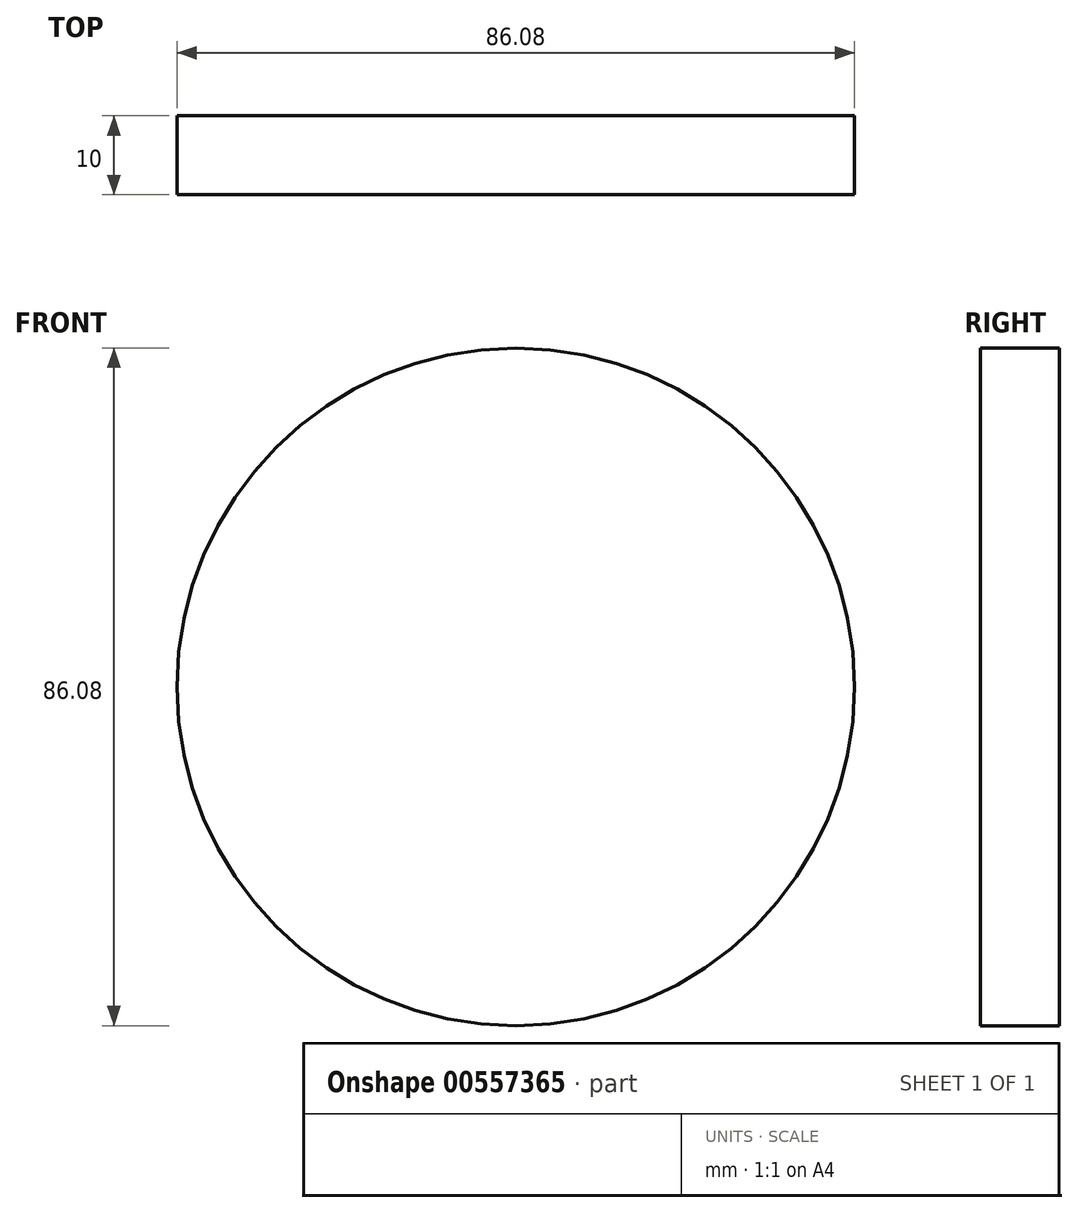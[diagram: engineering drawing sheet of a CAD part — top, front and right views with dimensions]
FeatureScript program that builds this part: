
annotation { "Feature Type Name" : "Feature", "Feature Type Description" : "" }
export const myFeature = defineFeature(function(context is Context, id is Id, definition is map)
    precondition{}
    {
        {
            var Q0;
            Q0=qCreatedBy(makeId("Front.planeOp"),FACE);
            var sketch = newSketch(context, id + "F0", { "sketchPlane" : qUnion([Q0])});
            skCircle(sketch, "E0", {"center": v(0, 0) * mm, "radius": 43.04 * mm});
            skSolve(sketch);
        }
        {
            var Q0;
            Q0=sQuery(id+"F0.wireOp",EDGE,"E0");
            extrude(context, id + "F1", {"bodyType" : ToolBodyType.SURFACE, "surfaceEntities" : qUnion([Q0]), "depth" : 10 * mm, "offsetDistance" : 25.4 * mm});
        }
    });
